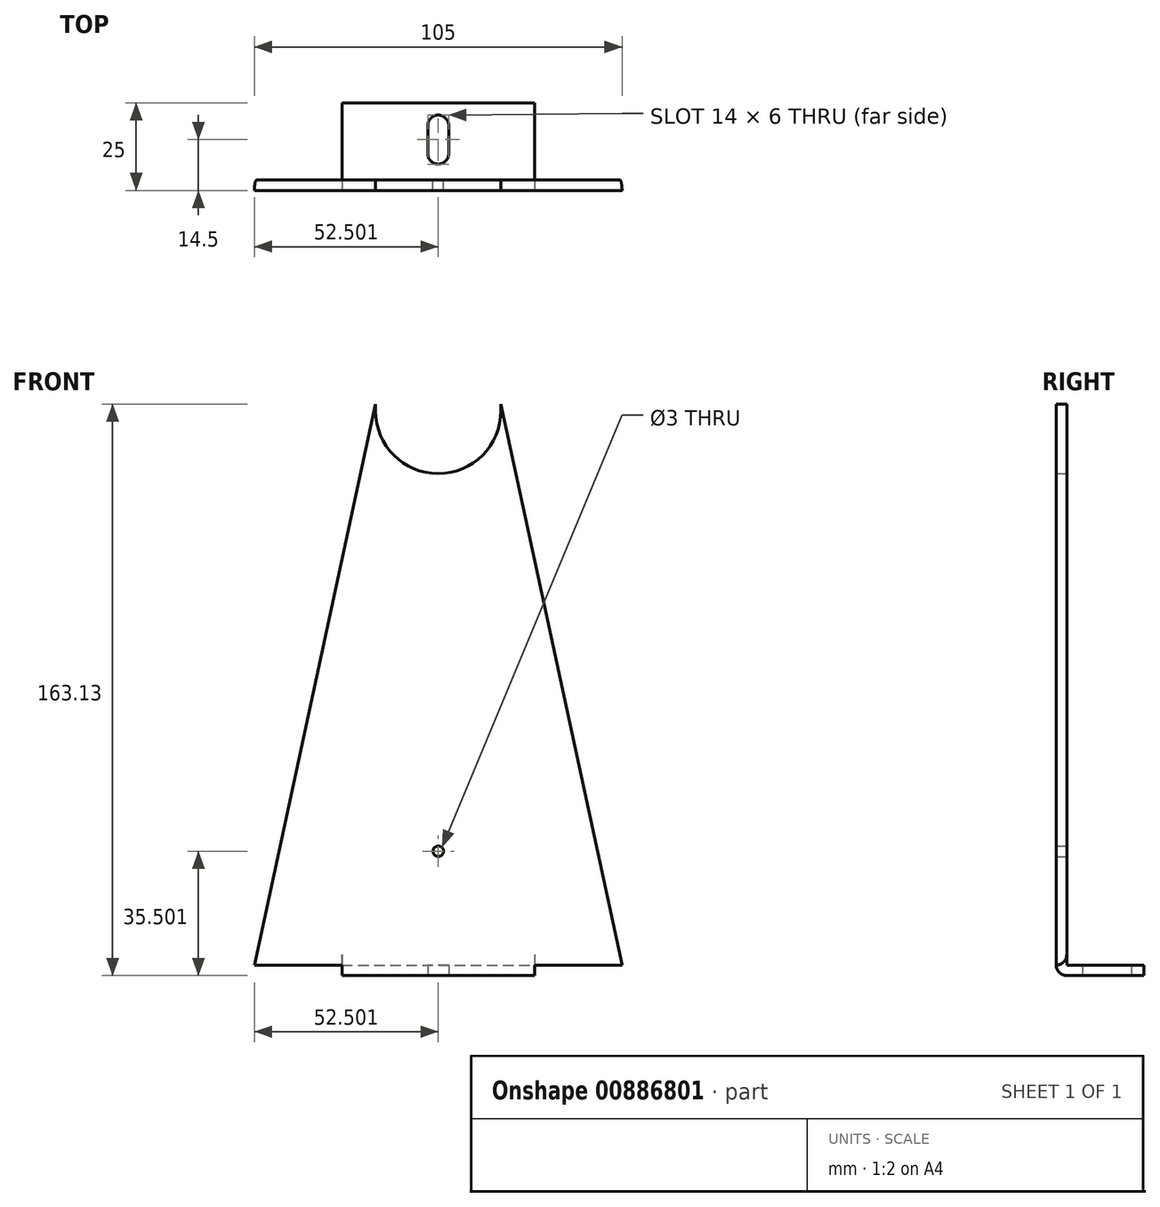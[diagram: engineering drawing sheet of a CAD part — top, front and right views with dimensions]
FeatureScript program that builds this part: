
annotation { "Feature Type Name" : "Feature", "Feature Type Description" : "" }
export const myFeature = defineFeature(function(context is Context, id is Id, definition is map)
    precondition{}
    {
        {
            var Q0;
            Q0=qCreatedBy(makeId("Front.planeOp"),FACE);
            var sketch = newSketch(context, id + "F0", { "sketchPlane" : qUnion([Q0])});
            skCircle(sketch, "E0", {"center": v(1053.9, -134.2) * mm, "radius": 17 * mm, "construction": true});
            skLineSegment(sketch, "E1", {"start": v(1680.14, -90.33) * mm, "end": v(1488.5, 408.9) * mm, "construction": true});
            skCircle(sketch, "E2", {"center": v(1053.9, -134.2) * mm, "radius": 21.5 * mm, "construction": true});
            skLineSegment(sketch, "E3", {"start": v(600.85, -74.2) * mm, "end": v(1722.15, -74.2) * mm, "construction": true});
            skLineSegment(sketch, "E4", {"start": v(549.42, 30.42) * mm, "end": v(557.61, 24.68) * mm, "construction": true});
            skLineSegment(sketch, "E5", {"start": v(556.15, 25.16) * mm, "end": v(512.34, -39.07) * mm, "construction": true});
            skLineSegment(sketch, "E6", {"start": v(553.17, 27) * mm, "end": v(509.45, -37.1) * mm, "construction": true});
            skLineSegment(sketch, "E7", {"start": v(550.2, 28.85) * mm, "end": v(506.56, -35.12) * mm, "construction": true});
            skLineSegment(sketch, "E8", {"start": v(506.6, -35.05) * mm, "end": v(512.39, -39) * mm, "construction": true});
            skLineSegment(sketch, "E9", {"start": v(570.93, 38.38) * mm, "end": v(557.61, 24.68) * mm, "construction": true});
            skLineSegment(sketch, "E10", {"start": v(552.29, 40.23) * mm, "end": v(549.42, 30.42) * mm, "construction": true});
            skLineSegment(sketch, "E11", {"start": v(600.85, -74.2) * mm, "end": v(440.53, 35.16) * mm, "construction": true});
            skLineSegment(sketch, "E12", {"start": v(713.05, 305.42) * mm, "end": v(656.4, 344.07) * mm, "construction": true});
            skLineSegment(sketch, "E13", {"start": v(702.52, 301.1) * mm, "end": v(656.02, 332.82) * mm, "construction": true});
            skLineSegment(sketch, "E14", {"start": v(710.06, 318.96) * mm, "end": v(669.92, 346.34) * mm, "construction": true});
            skLineSegment(sketch, "E15", {"start": v(689.46, 276.92) * mm, "end": v(655.21, 300.28) * mm, "construction": true});
            skLineSegment(sketch, "E16", {"start": v(615.02, -14.4) * mm, "end": v(402.92, 130.27) * mm, "construction": true});
            skLineSegment(sketch, "E17", {"start": v(559.84, 45.15) * mm, "end": v(550.25, 28.9) * mm, "construction": true});
            skLineSegment(sketch, "E18", {"start": v(562.86, 43.37) * mm, "end": v(553.2, 26.99) * mm, "construction": true});
            skLineSegment(sketch, "E19", {"start": v(565.87, 41.59) * mm, "end": v(556.13, 25.08) * mm, "construction": true});
            skLineSegment(sketch, "E20", {"start": v(565.87, 41.59) * mm, "end": v(559.84, 45.15) * mm, "construction": true});
            skLineSegment(sketch, "E21", {"start": v(472.04, 13.66) * mm, "end": v(769.02, 448.32) * mm, "construction": true});
            skArc(sketch, "E22", {"start": v(1006.96, -304.39) * mm, "mid": v(1011.65, -296.38) * mm, "end": v(1009.48, -287.35) * mm, "construction": true});
            skLineSegment(sketch, "E23", {"start": v(1053.9, -134.2) * mm, "end": v(1026.77, -317.41) * mm, "construction": true});
            skLineSegment(sketch, "E24", {"start": v(919.77, -241.35) * mm, "end": v(912.74, -288.83) * mm, "construction": true});
            skLineSegment(sketch, "E25", {"start": v(652.5, -164.98) * mm, "end": v(650.65, -171.73) * mm, "construction": true});
            skLineSegment(sketch, "E26", {"start": v(1031.93, -282.2) * mm, "end": v(579.95, -215.37) * mm, "construction": true});
            skLineSegment(sketch, "E27", {"start": v(674.61, -285.96) * mm, "end": v(640.98, -281) * mm, "construction": true});
            skLineSegment(sketch, "E28", {"start": v(675.34, -281.02) * mm, "end": v(641.71, -276.04) * mm, "construction": true});
            skLineSegment(sketch, "E29", {"start": v(1058.23, -251.72) * mm, "end": v(1048.27, -318.98) * mm, "construction": true});
            skLineSegment(sketch, "E30", {"start": v(945.2, -240.52) * mm, "end": v(983.81, -252.86) * mm, "construction": true});
            skLineSegment(sketch, "E31", {"start": v(941.1, -296.9) * mm, "end": v(949.25, -241.81) * mm, "construction": true});
            skLineSegment(sketch, "E32", {"start": v(941.66, -296.89) * mm, "end": v(949.79, -241.98) * mm, "construction": true});
            skLineSegment(sketch, "E33", {"start": v(973.82, -296.4) * mm, "end": v(980.43, -251.78) * mm, "construction": true});
            skLineSegment(sketch, "E34", {"start": v(972.56, -296.41) * mm, "end": v(979.23, -251.4) * mm, "construction": true});
            skLineSegment(sketch, "E35", {"start": v(964.98, -243.46) * mm, "end": v(956.63, -299.87) * mm, "construction": true});
            skLineSegment(sketch, "E36", {"start": v(983.81, -252.86) * mm, "end": v(977.37, -296.34) * mm, "construction": true});
            skLineSegment(sketch, "E37", {"start": v(945.2, -240.52) * mm, "end": v(936.84, -296.96) * mm, "construction": true});
            skLineSegment(sketch, "E38", {"start": v(979.95, -251.62) * mm, "end": v(973.32, -296.4) * mm, "construction": true});
            skLineSegment(sketch, "E39", {"start": v(949.06, -241.75) * mm, "end": v(940.9, -296.9) * mm, "construction": true});
            skLineSegment(sketch, "E40", {"start": v(940.66, -271.21) * mm, "end": v(945.36, -271.9) * mm, "construction": true});
            skLineSegment(sketch, "E41", {"start": v(944.62, -276.85) * mm, "end": v(939.93, -276.16) * mm, "construction": true});
            skLineSegment(sketch, "E42", {"start": v(946.27, -261.93) * mm, "end": v(942.12, -261.32) * mm, "construction": true});
            skLineSegment(sketch, "E43", {"start": v(940.8, -270.22) * mm, "end": v(945.5, -270.92) * mm, "construction": true});
            skLineSegment(sketch, "E44", {"start": v(941.39, -266.26) * mm, "end": v(946.09, -266.96) * mm, "construction": true});
            skLineSegment(sketch, "E45", {"start": v(941.24, -267.25) * mm, "end": v(945.94, -267.95) * mm, "construction": true});
            skArc(sketch, "E46", {"start": v(960.04, -276.86) * mm, "mid": v(966, -272.44) * mm, "end": v(961.58, -266.47) * mm, "construction": true});
            skArc(sketch, "E47", {"start": v(961.58, -266.47) * mm, "mid": v(955.61, -270.9) * mm, "end": v(960.04, -276.86) * mm, "construction": true});
            skLineSegment(sketch, "E48", {"start": v(1015.7, -245.42) * mm, "end": v(1005.73, -312.69) * mm, "construction": true});
            skLineSegment(sketch, "E49", {"start": v(1048.27, -318.98) * mm, "end": v(1005.73, -312.69) * mm, "construction": true});
            skLineSegment(sketch, "E50", {"start": v(1058.23, -251.72) * mm, "end": v(1015.7, -245.42) * mm, "construction": true});
            skArc(sketch, "E51", {"start": v(1011.94, -270.77) * mm, "mid": v(1016.63, -262.76) * mm, "end": v(1014.46, -253.73) * mm, "construction": true});
            skLineSegment(sketch, "E52", {"start": v(1037.98, -241.64) * mm, "end": v(948.95, -228.46) * mm, "construction": true});
            skLineSegment(sketch, "E53", {"start": v(576.43, -151.16) * mm, "end": v(632.5, -159.46) * mm, "construction": true});
            skLineSegment(sketch, "E54", {"start": v(575.4, -158.08) * mm, "end": v(631.06, -166.32) * mm, "construction": true});
            skLineSegment(sketch, "E55", {"start": v(575.3, -152) * mm, "end": v(574.56, -156.95) * mm, "construction": true});
            skArc(sketch, "E56", {"start": v(574.56, -156.95) * mm, "mid": v(574.75, -157.7) * mm, "end": v(575.4, -158.08) * mm, "construction": true});
            skArc(sketch, "E57", {"start": v(576.43, -151.16) * mm, "mid": v(575.69, -151.35) * mm, "end": v(575.3, -152) * mm, "construction": true});
            skLineSegment(sketch, "E58", {"start": v(631.06, -166.32) * mm, "end": v(650.65, -171.73) * mm, "construction": true});
            skLineSegment(sketch, "E59", {"start": v(632.5, -159.46) * mm, "end": v(652.5, -164.98) * mm, "construction": true});
            skLineSegment(sketch, "E60", {"start": v(600.85, -74.2) * mm, "end": v(567.5, -299.5) * mm, "construction": true});
            skLineSegment(sketch, "E61", {"start": v(644.77, -80.7) * mm, "end": v(612.1, -301.34) * mm, "construction": true});
            skLineSegment(sketch, "E62", {"start": v(641.71, -276.04) * mm, "end": v(640.98, -281) * mm, "construction": true});
            skLineSegment(sketch, "E63", {"start": v(675.34, -281.02) * mm, "end": v(674.61, -285.96) * mm, "construction": true});
            skLineSegment(sketch, "E64", {"start": v(607.36, -8.75) * mm, "end": v(864.68, 368.48) * mm, "construction": true});
            skLineSegment(sketch, "E65", {"start": v(622.48, -20.32) * mm, "end": v(871.92, 345.36) * mm, "construction": true});
            skLineSegment(sketch, "E66", {"start": v(615.02, -14.4) * mm, "end": v(879.24, 372.95) * mm, "construction": true});
            skLineSegment(sketch, "E67", {"start": v(1053.9, -134.2) * mm, "end": v(865.03, 414.2) * mm, "construction": true});
            skLineSegment(sketch, "E68", {"start": v(1034.15, -125.7) * mm, "end": v(850, 409.01) * mm, "construction": true});
            skLineSegment(sketch, "E69", {"start": v(861.66, 381.3) * mm, "end": v(851.9, 409.67) * mm, "construction": true});
            skLineSegment(sketch, "E70", {"start": v(1064.21, -115.34) * mm, "end": v(880.07, 419.37) * mm, "construction": true});
            skLineSegment(sketch, "E71", {"start": v(1053.9, -134.2) * mm, "end": v(645.8, -73.78) * mm, "construction": true});
            skLineSegment(sketch, "E72", {"start": v(743.09, -99.4) * mm, "end": v(644.17, -84.76) * mm, "construction": true});
            skLineSegment(sketch, "E73", {"start": v(746.34, -77.44) * mm, "end": v(647.42, -62.8) * mm, "construction": true});
            skLineSegment(sketch, "E74", {"start": v(1035.36, -145.1) * mm, "end": v(841.66, -116.43) * mm, "construction": true});
            skLineSegment(sketch, "E75", {"start": v(1039.32, -118.4) * mm, "end": v(845.61, -89.72) * mm, "construction": true});
            skLineSegment(sketch, "E76", {"start": v(879.24, 372.95) * mm, "end": v(768.93, 448.19) * mm, "construction": true});
            skLineSegment(sketch, "E77", {"start": v(966.15, -134.86) * mm, "end": v(995.58, -139.21) * mm, "construction": true});
            skLineSegment(sketch, "E78", {"start": v(960.23, -139.03) * mm, "end": v(994.85, -144.16) * mm, "construction": true});
            skLineSegment(sketch, "E79", {"start": v(963.6, -143.58) * mm, "end": v(964.04, -140.6) * mm, "construction": true});
            skArc(sketch, "E80", {"start": v(959.64, -143) * mm, "mid": v(959.83, -143.73) * mm, "end": v(960.48, -144.13) * mm, "construction": true});
            skLineSegment(sketch, "E81", {"start": v(960.48, -144.13) * mm, "end": v(962.46, -144.42) * mm, "construction": true});
            skArc(sketch, "E82", {"start": v(962.46, -144.42) * mm, "mid": v(963.2, -144.23) * mm, "end": v(963.6, -143.58) * mm, "construction": true});
            skLineSegment(sketch, "E83", {"start": v(965.3, -133.72) * mm, "end": v(967.21, -120.86) * mm, "construction": true});
            skLineSegment(sketch, "E84", {"start": v(963, -120.24) * mm, "end": v(959.64, -143) * mm, "construction": true});
            skLineSegment(sketch, "E85", {"start": v(962.42, -124.2) * mm, "end": v(966.63, -124.82) * mm, "construction": true});
            skArc(sketch, "E86", {"start": v(965.17, -139.77) * mm, "mid": v(964.43, -139.95) * mm, "end": v(964.04, -140.6) * mm, "construction": true});
            skLineSegment(sketch, "E87", {"start": v(961.7, -129.14) * mm, "end": v(965.9, -129.76) * mm, "construction": true});
            skLineSegment(sketch, "E88", {"start": v(960.08, -126.38) * mm, "end": v(968.24, -127.58) * mm, "construction": true});
            skLineSegment(sketch, "E89", {"start": v(974.82, -141.2) * mm, "end": v(975.55, -136.25) * mm, "construction": true});
            skArc(sketch, "E90", {"start": v(965.3, -133.72) * mm, "mid": v(965.5, -134.46) * mm, "end": v(966.15, -134.86) * mm, "construction": true});
            skLineSegment(sketch, "E91", {"start": v(964.14, -119.4) * mm, "end": v(966.37, -119.73) * mm, "construction": true});
            skArc(sketch, "E92", {"start": v(964.14, -119.4) * mm, "mid": v(963.4, -119.58) * mm, "end": v(963, -120.24) * mm, "construction": true});
            skArc(sketch, "E93", {"start": v(967.21, -120.86) * mm, "mid": v(967.03, -120.12) * mm, "end": v(966.37, -119.73) * mm, "construction": true});
            skLineSegment(sketch, "E94", {"start": v(995.58, -139.21) * mm, "end": v(999.8, -144.9) * mm, "construction": true});
            skLineSegment(sketch, "E95", {"start": v(979.72, -143.94) * mm, "end": v(981.04, -135.04) * mm, "construction": true});
            skArc(sketch, "E96", {"start": v(995.7, -145.3) * mm, "mid": v(995.5, -144.55) * mm, "end": v(994.85, -144.16) * mm, "construction": true});
            skArc(sketch, "E97", {"start": v(995.25, -148.26) * mm, "mid": v(995.44, -149) * mm, "end": v(996.1, -149.4) * mm, "construction": true});
            skArc(sketch, "E98", {"start": v(998.07, -149.7) * mm, "mid": v(998.82, -149.5) * mm, "end": v(999.2, -148.85) * mm, "construction": true});
            skLineSegment(sketch, "E99", {"start": v(996.1, -149.4) * mm, "end": v(998.07, -149.7) * mm, "construction": true});
            skLineSegment(sketch, "E100", {"start": v(999.2, -148.85) * mm, "end": v(999.8, -144.9) * mm, "construction": true});
            skLineSegment(sketch, "E101", {"start": v(995.25, -148.26) * mm, "end": v(995.7, -145.3) * mm, "construction": true});
            skLineSegment(sketch, "E102", {"start": v(985.2, -142.73) * mm, "end": v(985.94, -137.79) * mm, "construction": true});
            skLineSegment(sketch, "E103", {"start": v(995.47, -146.78) * mm, "end": v(993.6, -159.38) * mm, "construction": true});
            skEllipticalArc(sketch, "E104", {"construction": true});
            skLineSegment(sketch, "E105", {"start": v(850, 409.01) * mm, "end": v(880.07, 419.37) * mm, "construction": true});
            skLineSegment(sketch, "E106", {"start": v(859.77, 380.65) * mm, "end": v(861.66, 381.3) * mm, "construction": true});
            skLineSegment(sketch, "E107", {"start": v(1053.92, -134.2) * mm, "end": v(1520.05, 326.73) * mm, "construction": true});
            skLineSegment(sketch, "E108", {"start": v(1075.4, -135.33) * mm, "end": v(1510.36, 294.78) * mm, "construction": true});
            skLineSegment(sketch, "E109", {"start": v(1060.7, -105.14) * mm, "end": v(1497.91, 327.2) * mm, "construction": true});
            skLineSegment(sketch, "E110", {"start": v(879.24, 372.95) * mm, "end": v(1502.3, 372.95) * mm, "construction": true});
            skLineSegment(sketch, "E111", {"start": v(901.53, 357.05) * mm, "end": v(1486.45, 357.05) * mm, "construction": true});
            skLineSegment(sketch, "E112", {"start": v(890.58, 388.85) * mm, "end": v(1474.25, 388.85) * mm, "construction": true});
            skArc(sketch, "E113", {"start": v(1486.5, 356.93) * mm, "mid": v(1487.54, 375.64) * mm, "end": v(1474.25, 388.85) * mm, "construction": true});
            skArc(sketch, "E114", {"start": v(890.58, 388.85) * mm, "mid": v(888.92, 370.5) * mm, "end": v(901.53, 357.05) * mm, "construction": true});
            skArc(sketch, "E115", {"start": v(1510.36, 294.78) * mm, "mid": v(1511.76, 313.92) * mm, "end": v(1497.91, 327.2) * mm, "construction": true});
            skLineSegment(sketch, "E116", {"start": v(1722.15, -74.2) * mm, "end": v(1680.14, -90.33) * mm, "construction": true});
            skLineSegment(sketch, "E117", {"start": v(915.6, -231.4) * mm, "end": v(630.6, -162.69) * mm, "construction": true});
            skLineSegment(sketch, "E118", {"start": v(913.6, -239.65) * mm, "end": v(801.39, -212.6) * mm, "construction": true});
            skLineSegment(sketch, "E119", {"start": v(917.6, -223.13) * mm, "end": v(805.37, -196.07) * mm, "construction": true});
            skArc(sketch, "E120", {"start": v(924, -233.74) * mm, "mid": v(919.82, -232.5) * mm, "end": v(915.6, -231.4) * mm, "construction": true});
            skArc(sketch, "E121", {"start": v(921.8, -241.96) * mm, "mid": v(917.73, -240.73) * mm, "end": v(913.6, -239.65) * mm, "construction": true});
            skArc(sketch, "E122", {"start": v(919.09, -223.5) * mm, "mid": v(918.34, -223.31) * mm, "end": v(917.6, -223.13) * mm, "construction": true});
            skLineSegment(sketch, "E123", {"start": v(631.26, -168.55) * mm, "end": v(633.85, -157.83) * mm, "construction": true});
            skLineSegment(sketch, "E124", {"start": v(1013.2, -262.25) * mm, "end": v(924, -233.74) * mm, "construction": true});
            skLineSegment(sketch, "E125", {"start": v(1011.94, -270.77) * mm, "end": v(921.42, -241.84) * mm, "construction": true});
            skLineSegment(sketch, "E126", {"start": v(1014.46, -253.73) * mm, "end": v(985.84, -244.58) * mm, "construction": true});
            skLineSegment(sketch, "E127", {"start": v(631.26, -168.55) * mm, "end": v(641.06, -174.4) * mm, "construction": true});
            skLineSegment(sketch, "E128", {"start": v(633.85, -157.83) * mm, "end": v(651.56, -156.6) * mm, "construction": true});
            skLineSegment(sketch, "E129", {"start": v(805.37, -196.07) * mm, "end": v(651.56, -156.6) * mm, "construction": true});
            skLineSegment(sketch, "E130", {"start": v(693.7, -188.3) * mm, "end": v(801.39, -212.6) * mm, "construction": true});
            skLineSegment(sketch, "E131", {"start": v(641.06, -174.4) * mm, "end": v(688.9, -185.2) * mm, "construction": true});
            skArc(sketch, "E132", {"start": v(905.87, -297.16) * mm, "mid": v(910.24, -297.33) * mm, "end": v(914.6, -297.34) * mm, "construction": true});
            skArc(sketch, "E133", {"start": v(906.36, -288.67) * mm, "mid": v(910.61, -288.83) * mm, "end": v(914.87, -288.83) * mm, "construction": true});
            skArc(sketch, "E134", {"start": v(905.39, -305.65) * mm, "mid": v(910.06, -305.83) * mm, "end": v(914.73, -305.84) * mm, "construction": true});
            skLineSegment(sketch, "E135", {"start": v(1008.18, -295.87) * mm, "end": v(914.6, -297.34) * mm, "construction": true});
            skLineSegment(sketch, "E136", {"start": v(1009.48, -287.35) * mm, "end": v(914.47, -288.84) * mm, "construction": true});
            skLineSegment(sketch, "E137", {"start": v(1006.96, -304.39) * mm, "end": v(914.73, -305.84) * mm, "construction": true});
            skLineSegment(sketch, "E138", {"start": v(688.9, -185.2) * mm, "end": v(693.7, -188.3) * mm, "construction": true});
            skArc(sketch, "E139", {"start": v(919.09, -223.5) * mm, "mid": v(951.5, -237.06) * mm, "end": v(985.84, -244.58) * mm, "construction": true});
            skLineSegment(sketch, "E140", {"start": v(936.85, -296.96) * mm, "end": v(977.38, -296.34) * mm, "construction": true});
            skFitSpline(sketch, "E141", {"points": [v(872.4, 346.08) * mm, v(876.18, 356.24) * mm, v(881.69, 371.02) * mm, v(868.73, 369.09) * mm, v(864.68, 368.48) * mm], "construction": true});
            skLineSegment(sketch, "E142", {"start": v(662.14, -86.28) * mm, "end": v(644.63, -83.68) * mm, "construction": true});
            skLineSegment(sketch, "E143", {"start": v(665.07, -66.5) * mm, "end": v(647.56, -63.9) * mm, "construction": true});
            skLineSegment(sketch, "E144", {"start": v(664.41, -84.6) * mm, "end": v(666.76, -68.76) * mm, "construction": true});
            skArc(sketch, "E145", {"start": v(662.14, -86.28) * mm, "mid": v(663.62, -85.9) * mm, "end": v(664.41, -84.6) * mm, "construction": true});
            skArc(sketch, "E146", {"start": v(666.76, -68.76) * mm, "mid": v(666.38, -67.28) * mm, "end": v(665.07, -66.5) * mm, "construction": true});
            skArc(sketch, "E147", {"start": v(591.11, -61.72) * mm, "mid": v(584.1, -63.16) * mm, "end": v(585.54, -70.17) * mm, "construction": true});
            skLineSegment(sketch, "E148", {"start": v(585.54, -70.17) * mm, "end": v(605.08, -83.05) * mm, "construction": true});
            skLineSegment(sketch, "E149", {"start": v(601.2, -91.02) * mm, "end": v(582.02, -84.5) * mm, "construction": true});
            skLineSegment(sketch, "E150", {"start": v(584.15, -63.19) * mm, "end": v(613.37, -82.46) * mm, "construction": true});
            skLineSegment(sketch, "E151", {"start": v(607.46, -8.63) * mm, "end": v(572.75, -54.03) * mm, "construction": true});
            skLineSegment(sketch, "E152", {"start": v(644.18, -84.66) * mm, "end": v(644.29, -83.94) * mm, "construction": true});
            skLineSegment(sketch, "E153", {"start": v(591.11, -61.72) * mm, "end": v(618.65, -79.88) * mm, "construction": true});
            skArc(sketch, "E154", {"start": v(618.65, -79.88) * mm, "mid": v(620.57, -80.9) * mm, "end": v(622.66, -81.47) * mm, "construction": true});
            skLineSegment(sketch, "E155", {"start": v(644.18, -84.66) * mm, "end": v(622.66, -81.47) * mm, "construction": true});
            skArc(sketch, "E156", {"start": v(644.63, -83.68) * mm, "mid": v(644.4, -83.74) * mm, "end": v(644.29, -83.94) * mm, "construction": true});
            skLineSegment(sketch, "E157", {"start": v(644.18, -84.66) * mm, "end": v(644.19, -84.63) * mm, "construction": true});
            skArc(sketch, "E158", {"start": v(601.2, -91.02) * mm, "mid": v(606.49, -88.67) * mm, "end": v(605.08, -83.05) * mm, "construction": true});
            skArc(sketch, "E159", {"start": v(617.78, -52.64) * mm, "mid": v(628.06, -58.54) * mm, "end": v(639.47, -61.73) * mm, "construction": true});
            skLineSegment(sketch, "E160", {"start": v(670.48, -77.43) * mm, "end": v(577.33, -63.64) * mm, "construction": true});
            skLineSegment(sketch, "E161", {"start": v(647.4, -62.9) * mm, "end": v(639.47, -61.73) * mm, "construction": true});
            skArc(sketch, "E162", {"start": v(647.3, -63.56) * mm, "mid": v(647.36, -63.78) * mm, "end": v(647.56, -63.9) * mm, "construction": true});
            skLineSegment(sketch, "E163", {"start": v(647.3, -63.56) * mm, "end": v(647.4, -62.9) * mm, "construction": true});
            skArc(sketch, "E164", {"start": v(614, -32.51) * mm, "mid": v(611.92, -43.32) * mm, "end": v(617.78, -52.64) * mm, "construction": true});
            skLineSegment(sketch, "E165", {"start": v(614, -32.51) * mm, "end": v(622.56, -20.17) * mm, "construction": true});
            skLineSegment(sketch, "E166", {"start": v(577.33, -63.64) * mm, "end": v(629.71, 4.8) * mm, "construction": true});
            skArc(sketch, "E167", {"start": v(598.7, -25.94) * mm, "mid": v(602.23, -29.14) * mm, "end": v(601.27, -24.48) * mm, "construction": true});
            skArc(sketch, "E168", {"start": v(572.75, -54.03) * mm, "mid": v(569.56, -71.65) * mm, "end": v(582.02, -84.5) * mm, "construction": true});
            skCircle(sketch, "E169", {"center": v(586.41, -46.03) * mm, "radius": 2 * mm, "construction": true});
            skArc(sketch, "E170", {"start": v(585.71, -43.63) * mm, "mid": v(585.82, -48.46) * mm, "end": v(588.14, -44.23) * mm, "construction": true});
            skArc(sketch, "E171", {"start": v(632.31, -4.97) * mm, "mid": v(632.7, -3.49) * mm, "end": v(631.94, -2.16) * mm, "construction": true});
            skLineSegment(sketch, "E172", {"start": v(608.84, -9.3) * mm, "end": v(619.6, 4.75) * mm, "construction": true});
            skLineSegment(sketch, "E173", {"start": v(621.55, -19.02) * mm, "end": v(632.31, -4.97) * mm, "construction": true});
            skLineSegment(sketch, "E174", {"start": v(607.46, -8.63) * mm, "end": v(608.42, -9.36) * mm, "construction": true});
            skArc(sketch, "E175", {"start": v(621.55, -19.02) * mm, "mid": v(621.5, -19.24) * mm, "end": v(621.6, -19.44) * mm, "construction": true});
            skLineSegment(sketch, "E176", {"start": v(621.6, -19.44) * mm, "end": v(622.56, -20.17) * mm, "construction": true});
            skCircle(sketch, "E177", {"center": v(601, -26.97) * mm, "radius": 2 * mm, "construction": true});
            skArc(sketch, "E178", {"start": v(608.42, -9.36) * mm, "mid": v(608.64, -9.42) * mm, "end": v(608.84, -9.3) * mm, "construction": true});
            skLineSegment(sketch, "E179", {"start": v(608.42, -9.36) * mm, "end": v(607.46, -8.63) * mm, "construction": true});
            skArc(sketch, "E180", {"start": v(622.4, 5.12) * mm, "mid": v(620.93, 5.52) * mm, "end": v(619.6, 4.75) * mm, "construction": true});
            skLineSegment(sketch, "E181", {"start": v(631.94, -2.16) * mm, "end": v(622.4, 5.12) * mm, "construction": true});
            skLineSegment(sketch, "E182", {"start": v(619.71, -24.29) * mm, "end": v(604.42, -12.6) * mm, "construction": true});
            skLineSegment(sketch, "E183", {"start": v(639.24, -83.93) * mm, "end": v(642.46, -62.17) * mm, "construction": true});
            skCircle(sketch, "E184", {"center": v(600.85, -74.2) * mm, "radius": 5 * mm, "construction": true});
            skLineSegment(sketch, "E185", {"start": v(621.6, -19.44) * mm, "end": v(608.42, -9.36) * mm, "construction": true});
            skLineSegment(sketch, "E186", {"start": v(644.29, -83.94) * mm, "end": v(647.3, -63.56) * mm, "construction": true});
            skLineSegment(sketch, "E187", {"start": v(841.66, -116.43) * mm, "end": v(743.09, -99.4) * mm, "construction": true});
            skLineSegment(sketch, "E188", {"start": v(746.34, -77.44) * mm, "end": v(845.61, -89.72) * mm, "construction": true});
            skEllipse(sketch, "E189", {"center": v(843.64, -103.07) * mm, "majorRadius": 13.5 * mm, "minorRadius": 8.5 * mm, "majorAxis": v(-0.15, -0.99), "construction": true});
            skCircle(sketch, "E190", {"center": v(645.8, -73.78) * mm, "radius": 11 * mm, "construction": true});
            skLineSegment(sketch, "E191", {"start": v(634.82, -284.6) * mm, "end": v(635, -277.6) * mm, "construction": true});
            skLineSegment(sketch, "E192", {"start": v(558, -275.8) * mm, "end": v(614.08, -284.09) * mm, "construction": true});
            skLineSegment(sketch, "E193", {"start": v(559.02, -268.88) * mm, "end": v(614.68, -277.1) * mm, "construction": true});
            skLineSegment(sketch, "E194", {"start": v(557.16, -274.67) * mm, "end": v(557.89, -269.73) * mm, "construction": true});
            skArc(sketch, "E195", {"start": v(559.02, -268.88) * mm, "mid": v(558.28, -269.07) * mm, "end": v(557.89, -269.73) * mm, "construction": true});
            skArc(sketch, "E196", {"start": v(557.16, -274.67) * mm, "mid": v(557.34, -275.42) * mm, "end": v(558, -275.8) * mm, "construction": true});
            skLineSegment(sketch, "E197", {"start": v(614.68, -277.1) * mm, "end": v(635, -277.6) * mm, "construction": true});
            skLineSegment(sketch, "E198", {"start": v(614.08, -284.09) * mm, "end": v(634.82, -284.6) * mm, "construction": true});
            skLineSegment(sketch, "E199", {"start": v(905.87, -297.16) * mm, "end": v(613.19, -280.45) * mm, "construction": true});
            skLineSegment(sketch, "E200", {"start": v(906.36, -288.67) * mm, "end": v(791.11, -282.1) * mm, "construction": true});
            skLineSegment(sketch, "E201", {"start": v(905.39, -305.65) * mm, "end": v(790.14, -299.07) * mm, "construction": true});
            skLineSegment(sketch, "E202", {"start": v(615.52, -275.03) * mm, "end": v(614.89, -286.04) * mm, "construction": true});
            skLineSegment(sketch, "E203", {"start": v(615.52, -275.03) * mm, "end": v(632.73, -270.73) * mm, "construction": true});
            skLineSegment(sketch, "E204", {"start": v(614.89, -286.04) * mm, "end": v(631.5, -292.34) * mm, "construction": true});
            skLineSegment(sketch, "E205", {"start": v(790.14, -299.07) * mm, "end": v(631.5, -292.34) * mm, "construction": true});
            skLineSegment(sketch, "E206", {"start": v(632.73, -270.73) * mm, "end": v(791.11, -282.1) * mm, "construction": true});
            skLineSegment(sketch, "E207", {"start": v(703.93, 282.77) * mm, "end": v(553.52, 27.55) * mm, "construction": true});
            skArc(sketch, "E208", {"start": v(703.93, 282.77) * mm, "mid": v(707.75, 289.77) * mm, "end": v(711.1, 297.02) * mm, "construction": true});
            skArc(sketch, "E209", {"start": v(695.75, 287.6) * mm, "mid": v(699.27, 294.04) * mm, "end": v(702.35, 300.71) * mm, "construction": true});
            skArc(sketch, "E210", {"start": v(712.12, 277.95) * mm, "mid": v(716.24, 285.5) * mm, "end": v(719.85, 293.32) * mm, "construction": true});
            skLineSegment(sketch, "E211", {"start": v(712.12, 277.95) * mm, "end": v(570.93, 38.38) * mm, "construction": true});
            skLineSegment(sketch, "E212", {"start": v(695.75, 287.6) * mm, "end": v(578.7, 88.99) * mm, "construction": true});
            skLineSegment(sketch, "E213", {"start": v(577.7, 83.34) * mm, "end": v(552.29, 40.23) * mm, "construction": true});
            skLineSegment(sketch, "E214", {"start": v(764.21, 422.8) * mm, "end": v(711.1, 297.02) * mm, "construction": true});
            skLineSegment(sketch, "E215", {"start": v(781.6, 439.55) * mm, "end": v(719.85, 293.32) * mm, "construction": true});
            skLineSegment(sketch, "E216", {"start": v(758.12, 432.79) * mm, "end": v(702.35, 300.71) * mm, "construction": true});
            skLineSegment(sketch, "E217", {"start": v(452.18, 96.19) * mm, "end": v(408.28, 32.03) * mm, "construction": true});
            skLineSegment(sketch, "E218", {"start": v(454.99, 94.09) * mm, "end": v(411.17, 30.06) * mm, "construction": true});
            skLineSegment(sketch, "E219", {"start": v(457.79, 91.98) * mm, "end": v(414.05, 28.08) * mm, "construction": true});
            skLineSegment(sketch, "E220", {"start": v(414.1, 28.15) * mm, "end": v(408.33, 32.1) * mm, "construction": true});
            skLineSegment(sketch, "E221", {"start": v(577.7, 83.34) * mm, "end": v(578.7, 88.99) * mm, "construction": true});
            skCircle(sketch, "E222", {"center": v(795.03, 249.5) * mm, "radius": 9.5 * mm, "construction": true});
            skLineSegment(sketch, "E223", {"start": v(789.96, 238.43) * mm, "end": v(790.5, 237.46) * mm, "construction": true});
            skLineSegment(sketch, "E224", {"start": v(796.05, 242.82) * mm, "end": v(795.76, 244.37) * mm, "construction": true});
            skLineSegment(sketch, "E225", {"start": v(789.82, 248.52) * mm, "end": v(790.17, 248.58) * mm, "construction": true});
            skLineSegment(sketch, "E226", {"start": v(796.02, 244.3) * mm, "end": v(789.82, 248.52) * mm, "construction": true});
            skLineSegment(sketch, "E227", {"start": v(784, 242.2) * mm, "end": v(792.26, 236.56) * mm, "construction": true});
            skLineSegment(sketch, "E228", {"start": v(792.26, 236.56) * mm, "end": v(793.8, 238.84) * mm, "construction": true});
            skLineSegment(sketch, "E229", {"start": v(791.91, 236.5) * mm, "end": v(792.26, 236.56) * mm, "construction": true});
            skLineSegment(sketch, "E230", {"start": v(784.06, 241.85) * mm, "end": v(784, 242.2) * mm, "construction": true});
            skLineSegment(sketch, "E231", {"start": v(795.95, 244.64) * mm, "end": v(790.17, 248.58) * mm, "construction": true});
            skLineSegment(sketch, "E232", {"start": v(786.57, 240.74) * mm, "end": v(789.96, 238.43) * mm, "construction": true});
            skLineSegment(sketch, "E233", {"start": v(791.91, 236.5) * mm, "end": v(784.06, 241.85) * mm, "construction": true});
            skLineSegment(sketch, "E234", {"start": v(786.58, 243.77) * mm, "end": v(789.82, 248.52) * mm, "construction": true});
            skLineSegment(sketch, "E235", {"start": v(787.99, 239.18) * mm, "end": v(793.06, 246.61) * mm, "construction": true});
            skLineSegment(sketch, "E236", {"start": v(786.39, 240.48) * mm, "end": v(791.18, 247.5) * mm, "construction": true});
            skLineSegment(sketch, "E237", {"start": v(786.08, 240.81) * mm, "end": v(791, 248.02) * mm, "construction": true});
            skLineSegment(sketch, "E238", {"start": v(786.57, 240.74) * mm, "end": v(785.47, 240.9) * mm, "construction": true});
            skLineSegment(sketch, "E239", {"start": v(789.96, 238.43) * mm, "end": v(794.75, 245.46) * mm, "construction": true});
            skLineSegment(sketch, "E240", {"start": v(790.2, 238) * mm, "end": v(795.12, 245.2) * mm, "construction": true});
            skLineSegment(sketch, "E241", {"start": v(784, 242.2) * mm, "end": v(785.55, 244.47) * mm, "construction": true});
            skLineSegment(sketch, "E242", {"start": v(793.8, 238.84) * mm, "end": v(785.55, 244.47) * mm, "construction": true});
            skLineSegment(sketch, "E243", {"start": v(792.78, 239.54) * mm, "end": v(796.02, 244.3) * mm, "construction": true});
            skArc(sketch, "E244", {"start": v(962.06, -126.67) * mm, "mid": v(930.44, 82.62) * mm, "end": v(787.99, 239.18) * mm, "construction": true});
            skLineSegment(sketch, "E245", {"start": v(679.65, 313.68) * mm, "end": v(680.2, 312.7) * mm, "construction": true});
            skLineSegment(sketch, "E246", {"start": v(685.7, 319.54) * mm, "end": v(685.64, 319.88) * mm, "construction": true});
            skLineSegment(sketch, "E247", {"start": v(679.5, 323.76) * mm, "end": v(679.86, 323.83) * mm, "construction": true});
            skLineSegment(sketch, "E248", {"start": v(685.7, 319.54) * mm, "end": v(679.5, 323.76) * mm, "construction": true});
            skLineSegment(sketch, "E249", {"start": v(673.69, 317.44) * mm, "end": v(681.95, 311.8) * mm, "construction": true});
            skLineSegment(sketch, "E250", {"start": v(681.95, 311.8) * mm, "end": v(683.5, 314.08) * mm, "construction": true});
            skLineSegment(sketch, "E251", {"start": v(681.6, 311.74) * mm, "end": v(681.95, 311.8) * mm, "construction": true});
            skLineSegment(sketch, "E252", {"start": v(673.75, 317.1) * mm, "end": v(673.69, 317.44) * mm, "construction": true});
            skLineSegment(sketch, "E253", {"start": v(685.64, 319.88) * mm, "end": v(679.86, 323.83) * mm, "construction": true});
            skLineSegment(sketch, "E254", {"start": v(676.27, 315.99) * mm, "end": v(679.65, 313.68) * mm, "construction": true});
            skLineSegment(sketch, "E255", {"start": v(681.6, 311.74) * mm, "end": v(673.75, 317.1) * mm, "construction": true});
            skLineSegment(sketch, "E256", {"start": v(676.27, 319.01) * mm, "end": v(679.5, 323.76) * mm, "construction": true});
            skLineSegment(sketch, "E257", {"start": v(677.68, 314.42) * mm, "end": v(682.75, 321.86) * mm, "construction": true});
            skLineSegment(sketch, "E258", {"start": v(676.27, 315.99) * mm, "end": v(681.05, 323.01) * mm, "construction": true});
            skLineSegment(sketch, "E259", {"start": v(675.77, 316.06) * mm, "end": v(680.68, 323.26) * mm, "construction": true});
            skLineSegment(sketch, "E260", {"start": v(676.27, 315.99) * mm, "end": v(675.16, 316.14) * mm, "construction": true});
            skLineSegment(sketch, "E261", {"start": v(679.65, 313.68) * mm, "end": v(684.44, 320.7) * mm, "construction": true});
            skLineSegment(sketch, "E262", {"start": v(679.9, 313.24) * mm, "end": v(684.81, 320.45) * mm, "construction": true});
            skLineSegment(sketch, "E263", {"start": v(673.69, 317.44) * mm, "end": v(675.24, 319.72) * mm, "construction": true});
            skLineSegment(sketch, "E264", {"start": v(683.5, 314.08) * mm, "end": v(675.24, 319.72) * mm, "construction": true});
            skLineSegment(sketch, "E265", {"start": v(682.47, 314.79) * mm, "end": v(685.7, 319.54) * mm, "construction": true});
            skArc(sketch, "E266", {"start": v(702.52, 301.1) * mm, "mid": v(708.88, 308.94) * mm, "end": v(710.06, 318.96) * mm, "construction": true});
            skArc(sketch, "E267", {"start": v(669.92, 346.34) * mm, "mid": v(661, 341.6) * mm, "end": v(656.02, 332.82) * mm, "construction": true});
            skArc(sketch, "E268", {"start": v(699, -121.18) * mm, "mid": v(709.07, -114.4) * mm, "end": v(703.24, -103.77) * mm, "construction": true});
            skArc(sketch, "E269", {"start": v(666.37, -98.3) * mm, "mid": v(657.7, -106.8) * mm, "end": v(665.37, -116.2) * mm, "construction": true});
            skLineSegment(sketch, "E270", {"start": v(699, -121.18) * mm, "end": v(665.37, -116.2) * mm, "construction": true});
            skLineSegment(sketch, "E271", {"start": v(701.91, -101.58) * mm, "end": v(702.96, -94.48) * mm, "construction": true});
            skLineSegment(sketch, "E272", {"start": v(668.28, -96.6) * mm, "end": v(669.33, -89.5) * mm, "construction": true});
            skLineSegment(sketch, "E273", {"start": v(667.15, -104.24) * mm, "end": v(700.78, -109.21) * mm, "construction": true});
            skLineSegment(sketch, "E274", {"start": v(666.24, -110.37) * mm, "end": v(699.87, -115.35) * mm, "construction": true});
            skLineSegment(sketch, "E275", {"start": v(703.4, -112.74) * mm, "end": v(663.63, -106.85) * mm, "construction": true});
            skArc(sketch, "E276", {"start": v(667.15, -104.24) * mm, "mid": v(663.63, -106.85) * mm, "end": v(666.24, -110.37) * mm, "construction": true});
            skArc(sketch, "E277", {"start": v(666.37, -98.3) * mm, "mid": v(667.63, -97.8) * mm, "end": v(668.28, -96.6) * mm, "construction": true});
            skArc(sketch, "E278", {"start": v(699.87, -115.35) * mm, "mid": v(703.4, -112.74) * mm, "end": v(700.78, -109.21) * mm, "construction": true});
            skArc(sketch, "E279", {"start": v(701.91, -101.58) * mm, "mid": v(702.18, -102.91) * mm, "end": v(703.24, -103.77) * mm, "construction": true});
            skLineSegment(sketch, "E280", {"start": v(702.12, -93.34) * mm, "end": v(670.46, -88.65) * mm, "construction": true});
            skArc(sketch, "E281", {"start": v(670.46, -88.65) * mm, "mid": v(669.72, -88.84) * mm, "end": v(669.33, -89.5) * mm, "construction": true});
            skArc(sketch, "E282", {"start": v(702.96, -94.48) * mm, "mid": v(702.78, -93.73) * mm, "end": v(702.12, -93.34) * mm, "construction": true});
            skCircle(sketch, "E283", {"center": v(1054.53, -129.2) * mm, "radius": 89.9 * mm, "construction": true});
            skCircle(sketch, "E284", {"center": v(600.85, -74.2) * mm, "radius": 41.4 * mm, "construction": true});
            skLineSegment(sketch, "E285", {"start": v(1055.81, -39.3) * mm, "end": v(601.44, -32.8) * mm, "construction": true});
            skLineSegment(sketch, "E286", {"start": v(459.53, 91.84) * mm, "end": v(451.2, 97.38) * mm, "construction": true});
            skLineSegment(sketch, "E287", {"start": v(459.13, 114.77) * mm, "end": v(451.2, 97.38) * mm, "construction": true});
            skLineSegment(sketch, "E288", {"start": v(462.18, 93.88) * mm, "end": v(459.53, 91.84) * mm, "construction": true});
            skArc(sketch, "E289", {"start": v(462.18, 93.88) * mm, "mid": v(473.4, 103.7) * mm, "end": v(483.33, 114.82) * mm, "construction": true});
            skLineSegment(sketch, "E290", {"start": v(469.46, 106.9) * mm, "end": v(457.81, 92.06) * mm, "construction": true});
            skLineSegment(sketch, "E291", {"start": v(466.7, 109.06) * mm, "end": v(454.96, 94.1) * mm, "construction": true});
            skLineSegment(sketch, "E292", {"start": v(463.96, 111.22) * mm, "end": v(452.12, 96.14) * mm, "construction": true});
            skLineSegment(sketch, "E293", {"start": v(463.96, 111.22) * mm, "end": v(469.46, 106.9) * mm, "construction": true});
            skLineSegment(sketch, "E294", {"start": v(638.46, 327.51) * mm, "end": v(455.36, 94.61) * mm, "construction": true});
            skArc(sketch, "E295", {"start": v(649.12, 339.36) * mm, "mid": v(643.6, 333.61) * mm, "end": v(638.46, 327.51) * mm, "construction": true});
            skArc(sketch, "E296", {"start": v(655.75, 332.55) * mm, "mid": v(650.65, 327.26) * mm, "end": v(645.92, 321.64) * mm, "construction": true});
            skArc(sketch, "E297", {"start": v(637.86, 341.42) * mm, "mid": v(634.34, 337.47) * mm, "end": v(630.99, 333.38) * mm, "construction": true});
            skLineSegment(sketch, "E298", {"start": v(630.99, 333.38) * mm, "end": v(459.13, 114.77) * mm, "construction": true});
            skLineSegment(sketch, "E299", {"start": v(645.92, 321.64) * mm, "end": v(483.33, 114.82) * mm, "construction": true});
            skLineSegment(sketch, "E300", {"start": v(746.99, 434.56) * mm, "end": v(649.12, 339.36) * mm, "construction": true});
            skLineSegment(sketch, "E301", {"start": v(756.26, 456.83) * mm, "end": v(636.32, 340.16) * mm, "construction": true});
            skLineSegment(sketch, "E302", {"start": v(758.51, 432.52) * mm, "end": v(655.75, 332.55) * mm, "construction": true});
            skLineSegment(sketch, "E303", {"start": v(1469.36, 401.56) * mm, "end": v(1507.64, 416.26) * mm, "construction": true});
            skLineSegment(sketch, "E304", {"start": v(1507.64, 416.26) * mm, "end": v(1552.44, 299.56) * mm, "construction": true});
            skLineSegment(sketch, "E305", {"start": v(1552.44, 299.56) * mm, "end": v(1514.16, 284.87) * mm, "construction": true});
            skLineSegment(sketch, "E306", {"start": v(1514.16, 284.87) * mm, "end": v(1469.36, 401.56) * mm, "construction": true});
            skLineSegment(sketch, "E307", {"start": v(844.6, 337.76) * mm, "end": v(883.44, 311.27) * mm, "construction": true});
            skLineSegment(sketch, "E308", {"start": v(844.6, 337.76) * mm, "end": v(836.16, 325.37) * mm, "construction": true});
            skLineSegment(sketch, "E309", {"start": v(836.16, 325.37) * mm, "end": v(874.98, 298.88) * mm, "construction": true});
            skLineSegment(sketch, "E310", {"start": v(874.98, 298.88) * mm, "end": v(883.44, 311.27) * mm, "construction": true});
            skLineSegment(sketch, "E311", {"start": v(864.68, 368.48) * mm, "end": v(778.96, 242.82) * mm, "construction": true});
            skLineSegment(sketch, "E312", {"start": v(864.68, 368.48) * mm, "end": v(862.2, 370.17) * mm, "construction": true});
            skLineSegment(sketch, "E313", {"start": v(862.2, 370.17) * mm, "end": v(776.49, 244.51) * mm, "construction": true});
            skLineSegment(sketch, "E314", {"start": v(776.49, 244.51) * mm, "end": v(778.96, 242.82) * mm, "construction": true});
            skLineSegment(sketch, "E315", {"start": v(853.45, 313.52) * mm, "end": v(871.62, 301.13) * mm, "construction": true});
            skLineSegment(sketch, "E316", {"start": v(853.45, 313.52) * mm, "end": v(798.8, 233.4) * mm, "construction": true});
            skLineSegment(sketch, "E317", {"start": v(798.8, 233.4) * mm, "end": v(816.96, 221) * mm, "construction": true});
            skLineSegment(sketch, "E318", {"start": v(816.96, 221) * mm, "end": v(871.62, 301.13) * mm, "construction": true});
            skLineSegment(sketch, "E319", {"start": v(776.49, 244.51) * mm, "end": v(796.31, 230.99) * mm, "construction": true});
            skLineSegment(sketch, "E320", {"start": v(774.8, 242.03) * mm, "end": v(794.62, 228.5) * mm, "construction": true});
            skLineSegment(sketch, "E321", {"start": v(776.49, 244.51) * mm, "end": v(774.8, 242.03) * mm, "construction": true});
            skLineSegment(sketch, "E322", {"start": v(794.62, 228.5) * mm, "end": v(796.31, 230.99) * mm, "construction": true});
            skLineSegment(sketch, "E323", {"start": v(658.17, 327.73) * mm, "end": v(712.83, 407.86) * mm, "construction": true});
            skLineSegment(sketch, "E324", {"start": v(712.83, 407.86) * mm, "end": v(751.65, 381.38) * mm, "construction": true});
            skLineSegment(sketch, "E325", {"start": v(751.65, 381.38) * mm, "end": v(697, 301.24) * mm, "construction": true});
            skLineSegment(sketch, "E326", {"start": v(697, 301.24) * mm, "end": v(658.17, 327.73) * mm, "construction": true});
            skPoint(sketch, "E327", {"position": v(677.58, 314.49) * mm});
            skLineSegment(sketch, "E328", {"start": v(721.15, 402.18) * mm, "end": v(743.45, 386.97) * mm, "construction": true});
            skLineSegment(sketch, "E329", {"start": v(721.15, 402.18) * mm, "end": v(729.6, 414.58) * mm, "construction": true});
            skLineSegment(sketch, "E330", {"start": v(729.6, 414.58) * mm, "end": v(751.9, 399.36) * mm, "construction": true});
            skLineSegment(sketch, "E331", {"start": v(751.9, 399.36) * mm, "end": v(743.45, 386.97) * mm, "construction": true});
            skPoint(sketch, "E332", {"position": v(732.3, 394.58) * mm});
            skLineSegment(sketch, "E333", {"start": v(637.81, 341.61) * mm, "end": v(756.26, 456.83) * mm, "construction": true});
            skLineSegment(sketch, "E334", {"start": v(871.62, 301.13) * mm, "end": v(889.8, 288.73) * mm, "construction": true});
            skLineSegment(sketch, "E335", {"start": v(840.38, 331.56) * mm, "end": v(879.2, 305.08) * mm, "construction": true});
            skLineSegment(sketch, "E336", {"start": v(653.86, 330.67) * mm, "end": v(701.3, 298.3) * mm, "construction": true});
            skLineSegment(sketch, "E337", {"start": v(780.27, 244.74) * mm, "end": v(945.35, 132.13) * mm});
            skPoint(sketch, "E338", {"position": v(868.06, 356.57) * mm});
            skLineSegment(sketch, "E339", {"start": v(727.04, 386.88) * mm, "end": v(703.9, 402.65) * mm, "construction": true});
            skCircle(sketch, "E340", {"center": v(695.83, 341.2) * mm, "radius": 1.5 * mm, "construction": true});
            skLineSegment(sketch, "E341", {"start": v(706.12, 380.2) * mm, "end": v(728.42, 364.96) * mm, "construction": true});
            skLineSegment(sketch, "E342", {"start": v(706.12, 380.2) * mm, "end": v(679.61, 341.39) * mm, "construction": true});
            skLineSegment(sketch, "E343", {"start": v(679.61, 341.39) * mm, "end": v(701.9, 326.15) * mm, "construction": true});
            skLineSegment(sketch, "E344", {"start": v(701.9, 326.15) * mm, "end": v(728.42, 364.96) * mm, "construction": true});
            skLineSegment(sketch, "E345", {"start": v(692.87, 360.8) * mm, "end": v(715.16, 345.56) * mm, "construction": true});
            skLineSegment(sketch, "E346", {"start": v(769.02, 448.32) * mm, "end": v(727.69, 476.56) * mm, "construction": true});
            skLineSegment(sketch, "E347", {"start": v(781.6, 439.55) * mm, "end": v(718.29, 286.72) * mm, "construction": true});
            skLineSegment(sketch, "E348", {"start": v(756.26, 456.83) * mm, "end": v(781.6, 439.55) * mm, "construction": true});
            skLineSegment(sketch, "E349", {"start": v(653.86, 330.67) * mm, "end": v(637.81, 341.61) * mm, "construction": true});
            skLineSegment(sketch, "E350", {"start": v(701.3, 298.3) * mm, "end": v(718.29, 286.72) * mm, "construction": true});
            skLineSegment(sketch, "E351", {"start": v(701.3, 298.3) * mm, "end": v(699.6, 295.83) * mm, "construction": true});
            skLineSegment(sketch, "E352", {"start": v(699.6, 295.83) * mm, "end": v(652.17, 328.2) * mm, "construction": true});
            skLineSegment(sketch, "E353", {"start": v(652.17, 328.2) * mm, "end": v(653.86, 330.67) * mm, "construction": true});
            skLineSegment(sketch, "E354", {"start": v(454.83, 576.68) * mm, "end": v(420.23, 416.55) * mm});
            skLineSegment(sketch, "E355", {"start": v(420.23, 416.55) * mm, "end": v(495.95, 416.55) * mm});
            skLineSegment(sketch, "E356", {"start": v(525.23, 416.55) * mm, "end": v(490.64, 576.68) * mm});
            skLineSegment(sketch, "E357", {"start": v(472.73, 416.55) * mm, "end": v(472.73, 592.22) * mm, "construction": true});
            skArc(sketch, "E358", {"start": v(454.83, 574.77) * mm, "mid": v(472.73, 556.87) * mm, "end": v(490.64, 574.77) * mm});
            skLineSegment(sketch, "E359.trimOffspring", {"start": v(495.95, 416.55) * mm, "end": v(525.23, 416.55) * mm});
            skCircle(sketch, "E360", {"center": v(472.73, 449.05) * mm, "radius": 1.5 * mm});
            skLineSegment(sketch, "E361", {"start": v(454.83, 574.77) * mm, "end": v(454.83, 576.68) * mm});
            skLineSegment(sketch, "E362", {"start": v(472.73, 574.77) * mm, "end": v(454.83, 574.77) * mm, "construction": true});
            skPoint(sketch, "E363.orphan", {"position": v(455.23, 578.55) * mm});
            skLineSegment(sketch, "E364", {"start": v(472.73, 574.77) * mm, "end": v(490.64, 574.77) * mm, "construction": true});
            skLineSegment(sketch, "E365", {"start": v(490.64, 574.77) * mm, "end": v(490.64, 576.68) * mm});
            skPoint(sketch, "E366.orphan", {"position": v(490.23, 578.55) * mm});
            skPoint(sketch, "E367.start.orphan", {"position": v(445.73, 416.55) * mm});
            const initialGuessF0  = {"E104": [0.7690192550415708, 0.4483164196433211, -0.5771491899465747, -0.8166387282905536, 0.01628397008579135, 0.015337817466823316, 4.737460054654662, 1.577010981135067]};
            skSetInitialGuess(sketch, initialGuessF0);
            skSolve(sketch);
        }
        {
            var Q0;
            Q0=makeQuery(id+"F0.imprint","IMPRINT",FACE,{"disambiguationData":[TD([[makeQuery(id+"F0.imprint","IMPRINT",EDGE,{"derivedFrom":sQuery(id+"F0.wireOp",EDGE,"E354")}),1.0]])]});
            extrude(context, id + "F1", {"entities" : qUnion([Q0]), "depth" : 3 * mm, "offsetDistance" : 25 * mm});
        }
        {
            var Q0;
            Q0=makeQuery(id+"F1.opExtrude","CAP_FACE",FACE,{"disambiguationData":[OSD([sQuery(id+"F0.wireOp",EDGE,"E354"),sQuery(id+"F0.wireOp",EDGE,"E355"),sQuery(id+"F0.wireOp",EDGE,"E356"),sQuery(id+"F0.wireOp",EDGE,"E358"),sQuery(id+"F0.wireOp",EDGE,"E359.trimOffspring"),sQuery(id+"F0.wireOp",EDGE,"E360"),sQuery(id+"F0.wireOp",EDGE,"E361"),sQuery(id+"F0.wireOp",EDGE,"E365")])],"isStart":false});
            var sketch = newSketch(context, id + "F2", { "sketchPlane" : qUnion([Q0])});
            skLineSegment(sketch, "E368.bottom", {"start": v(445.23, 416.55) * mm, "end": v(500.23, 416.55) * mm});
            skLineSegment(sketch, "E368.top", {"start": v(445.23, 413.55) * mm, "end": v(500.23, 413.55) * mm});
            skLineSegment(sketch, "E368.left", {"start": v(445.23, 416.55) * mm, "end": v(445.23, 413.55) * mm});
            skLineSegment(sketch, "E368.right", {"start": v(500.23, 416.55) * mm, "end": v(500.23, 413.55) * mm});
            skSolve(sketch);
        }
        {
            var Q0;
            Q0=qSketchRegion(id+"F2",true);
            extrude(context, id + "F3", {"entities" : qUnion([Q0]), "operationType" : NewBodyOperationType.ADD, "oppositeDirection" : true, "depth" : 25 * mm, "offsetDistance" : 25 * mm});
        }
        {
            var Q0;
            {var subQ0=sQuery(id+"F0.wireOp",EDGE,"E359.trimOffspring");var subQ1=sQuery(id+"F0.wireOp",EDGE,"E355");Q0=makeQuery(id+"F3.boolean.opBoolean","SPLIT",EDGE,{"disambiguationData":[topologyDisambiguationEdgeConnected([makeQuery(id+"F1.opExtrude","CAP_FACE",FACE,{"disambiguationData":[OSD([sQuery(id+"F0.wireOp",EDGE,"E354"),subQ1,sQuery(id+"F0.wireOp",EDGE,"E356"),sQuery(id+"F0.wireOp",EDGE,"E358"),subQ0,sQuery(id+"F0.wireOp",EDGE,"E360"),sQuery(id+"F0.wireOp",EDGE,"E361"),sQuery(id+"F0.wireOp",EDGE,"E365")])],"isStart":true}),makeQuery(id+"F3.opExtrude","SWEPT_FACE",FACE,{"disambiguationData":[OSD([sQuery(id+"F2.wireOp",EDGE,"E368.bottom")])]})])],"derivedFrom":makeQuery(id+"F1.opExtrude","CAP_EDGE",EDGE,{"disambiguationData":[OSD([subQ1,subQ0])],"isStart":true})});}
            var Q1;
            Q1=makeQuery(id+"F3.opExtrude","CAP_EDGE",EDGE,{"disambiguationData":[OSD([sQuery(id+"F2.wireOp",EDGE,"E368.top")])],"isStart":true});
            fillet(context, id + "F4", {"entities" : qUnion([Q0, Q1]), "radius" : 3 * mm, "tangentPropagation" : true, "allowEdgeOverflow" : false});
        }
        {
            var Q0;
            Q0=makeQuery(id+"F3.opExtrude","SWEPT_FACE",FACE,{"disambiguationData":[OSD([sQuery(id+"F2.wireOp",EDGE,"E368.top")])]});
            var sketch = newSketch(context, id + "F5", { "sketchPlane" : qUnion([Q0])});
            skArc(sketch, "E369", {"start": v(475.73, -7.5) * mm, "mid": v(472.73, -4.5) * mm, "end": v(469.73, -7.5) * mm});
            skPoint(sketch, "E369.centerSnap0", {"position": v(472.73, 0) * mm});
            skLineSegment(sketch, "E370", {"start": v(469.73, -7.5) * mm, "end": v(469.73, -15.5) * mm});
            skLineSegment(sketch, "E371", {"start": v(475.73, -7.5) * mm, "end": v(475.73, -15.5) * mm});
            skArc(sketch, "E372", {"start": v(469.73, -15.5) * mm, "mid": v(472.73, -18.5) * mm, "end": v(475.73, -15.5) * mm});
            skSolve(sketch);
        }
        {
            var Q0;
            Q0=qSketchRegion(id+"F5",true);
            extrude(context, id + "F6", {"entities" : qUnion([Q0]), "operationType" : NewBodyOperationType.REMOVE, "endBound" : BoundingType.THROUGH_ALL, "oppositeDirection" : true, "depth" : 25 * mm, "offsetDistance" : 25 * mm});
        }
    });
